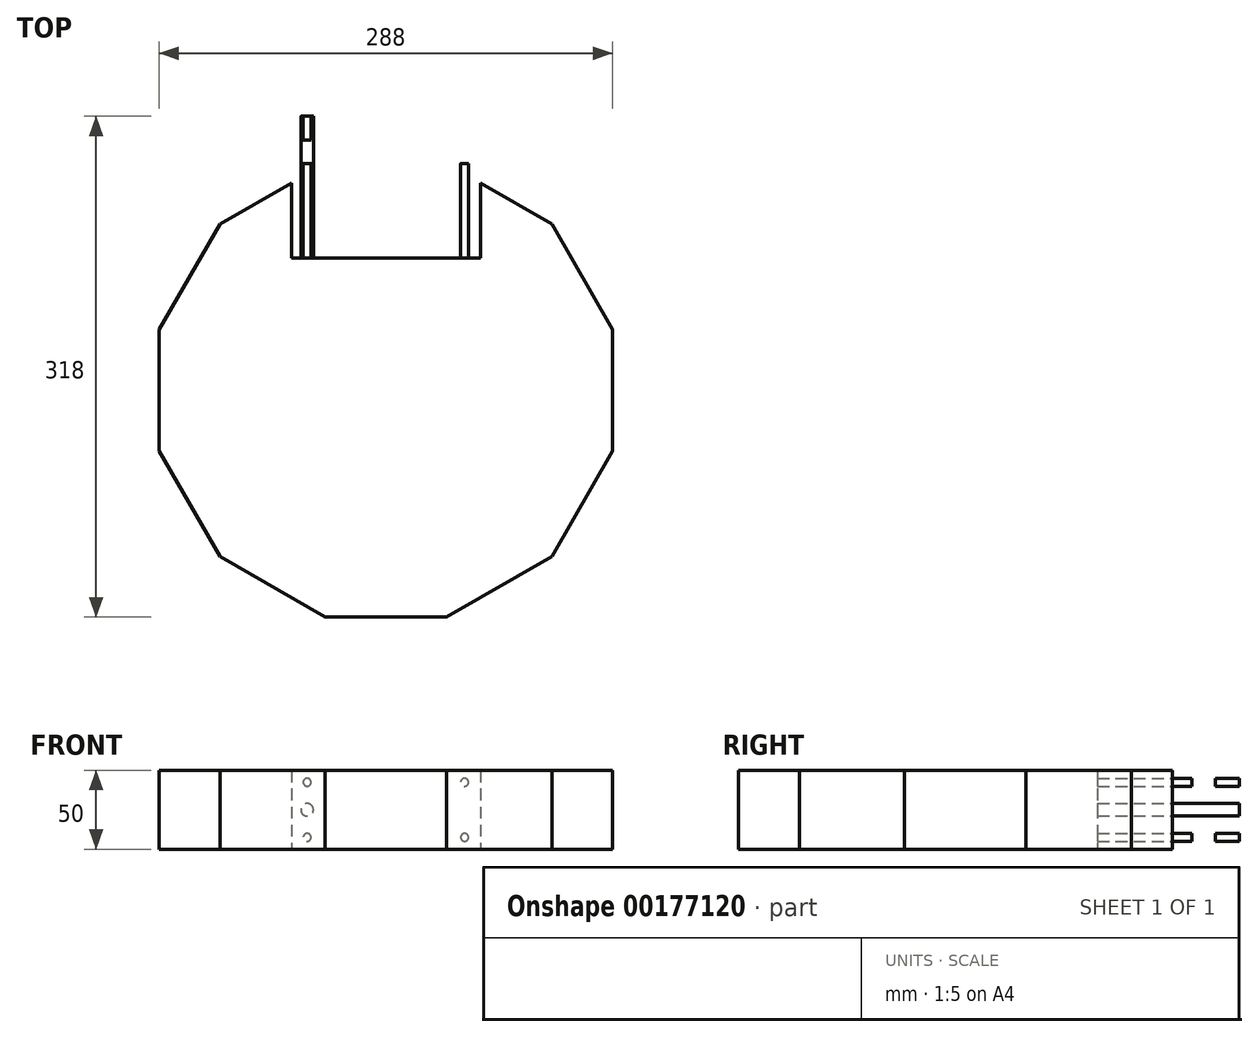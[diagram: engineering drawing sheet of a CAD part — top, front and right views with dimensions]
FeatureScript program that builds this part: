
annotation { "Feature Type Name" : "Feature", "Feature Type Description" : "" }
export const myFeature = defineFeature(function(context is Context, id is Id, definition is map)
    precondition{}
    {
        {
            var Q0;
            Q0=qCreatedBy(makeId("Top.planeOp"),FACE);
            var sketch = newSketch(context, id + "F0", { "sketchPlane" : qUnion([Q0])});
            skCircle(sketch, "E0.cCircle", {"center": v(0, 0) * mm, "radius": 144 * mm, "construction": true});
            skLineSegment(sketch, "E0.0", {"start": v(-38.58, 144) * mm, "end": v(38.58, 144) * mm, "construction": true});
            skLineSegment(sketch, "E0.1", {"start": v(38.58, 144) * mm, "end": v(105.42, 105.42) * mm, "construction": true});
            skLineSegment(sketch, "E0.2", {"start": v(105.42, 105.42) * mm, "end": v(144, 38.58) * mm});
            skLineSegment(sketch, "E0.3", {"start": v(144, 38.58) * mm, "end": v(144, -38.58) * mm});
            skLineSegment(sketch, "E0.4", {"start": v(144, -38.58) * mm, "end": v(105.42, -105.42) * mm});
            skLineSegment(sketch, "E0.5", {"start": v(105.42, -105.42) * mm, "end": v(38.58, -144) * mm});
            skLineSegment(sketch, "E0.6", {"start": v(38.58, -144) * mm, "end": v(-38.58, -144) * mm});
            skLineSegment(sketch, "E0.7", {"start": v(-38.58, -144) * mm, "end": v(-105.42, -105.42) * mm});
            skLineSegment(sketch, "E0.8", {"start": v(-105.42, -105.42) * mm, "end": v(-144, -38.58) * mm});
            skLineSegment(sketch, "E0.9", {"start": v(-144, -38.58) * mm, "end": v(-144, 38.58) * mm});
            skLineSegment(sketch, "E0.10", {"start": v(-144, 38.58) * mm, "end": v(-105.42, 105.42) * mm});
            skLineSegment(sketch, "E0.11", {"start": v(-105.42, 105.42) * mm, "end": v(-38.58, 144) * mm, "construction": true});
            skPoint(sketch, "E0.0.midPoint", {"position": v(0, 144) * mm});
            skLineSegment(sketch, "E1", {"start": v(-60, 174) * mm, "end": v(60, 174) * mm});
            skLineSegment(sketch, "E2", {"start": v(0, 0) * mm, "end": v(0, 217.16) * mm, "construction": true});
            skLineSegment(sketch, "E3", {"start": v(-60, 174) * mm, "end": v(-60, 131.64) * mm});
            skLineSegment(sketch, "E4", {"start": v(-60, 131.64) * mm, "end": v(-105.42, 105.42) * mm});
            skLineSegment(sketch, "E5", {"start": v(60, 174) * mm, "end": v(60, 131.64) * mm});
            skLineSegment(sketch, "E6", {"start": v(60, 131.64) * mm, "end": v(105.42, 105.42) * mm});
            skSolve(sketch);
        }
        {
            var Q0;
            Q0=makeQuery(id+"F0.imprint","IMPRINT",FACE,{"disambiguationData":[TD([[makeQuery(id+"F0.imprint","IMPRINT",EDGE,{"derivedFrom":sQuery(id+"F0.wireOp",EDGE,"E0.2")}),-1.0]])]});
            extrude(context, id + "F1", {"entities" : qUnion([Q0]), "depth" : 50 * mm});
        }
        {
            var Q0;
            Q0=makeQuery(id+"F1.opExtrude","CAP_FACE",FACE,{"disambiguationData":[OSD([sQuery(id+"F0.wireOp",EDGE,"E0.2"),sQuery(id+"F0.wireOp",EDGE,"E0.3"),sQuery(id+"F0.wireOp",EDGE,"E0.4"),sQuery(id+"F0.wireOp",EDGE,"E0.5"),sQuery(id+"F0.wireOp",EDGE,"E0.6"),sQuery(id+"F0.wireOp",EDGE,"E0.7"),sQuery(id+"F0.wireOp",EDGE,"E0.8"),sQuery(id+"F0.wireOp",EDGE,"E0.9"),sQuery(id+"F0.wireOp",EDGE,"E0.10"),sQuery(id+"F0.wireOp",EDGE,"E1"),sQuery(id+"F0.wireOp",EDGE,"E3"),sQuery(id+"F0.wireOp",EDGE,"E4"),sQuery(id+"F0.wireOp",EDGE,"E5"),sQuery(id+"F0.wireOp",EDGE,"E6")])],"isStart":false});
            var sketch = newSketch(context, id + "F2", { "sketchPlane" : qUnion([Q0])});
            skLineSegment(sketch, "E7", {"start": v(-60, 159) * mm, "end": v(-40, 159) * mm});
            skLineSegment(sketch, "E8", {"start": v(-60, 144) * mm, "end": v(-40, 144) * mm});
            skArc(sketch, "E9", {"start": v(-40, 144) * mm, "mid": v(-32.5, 151.5) * mm, "end": v(-40, 159) * mm});
            skLineSegment(sketch, "E10", {"start": v(-40, 159) * mm, "end": v(-40, 144) * mm, "construction": true});
            skLineSegment(sketch, "E11", {"start": v(-60, 151.5) * mm, "end": v(-40, 151.5) * mm, "construction": true});
            skLineSegment(sketch, "E12", {"start": v(-60, 159) * mm, "end": v(-60, 144) * mm});
            skLineSegment(sketch, "E13.MirrorCS", {"start": v(60, 159) * mm, "end": v(60, 144) * mm});
            skLineSegment(sketch, "E14.MirrorCS", {"start": v(60, 159) * mm, "end": v(40, 159) * mm});
            skArc(sketch, "E15.MirrorCS", {"start": v(40, 144) * mm, "mid": v(32.5, 151.5) * mm, "end": v(40, 159) * mm});
            skLineSegment(sketch, "E16.MirrorCS", {"start": v(60, 144) * mm, "end": v(40, 144) * mm});
            skCircle(sketch, "E17", {"center": v(0, 0) * mm, "radius": 87.5 * mm, "construction": true});
            skCircle(sketch, "E18", {"center": v(0, 87.5) * mm, "radius": 4 * mm});
            skCircle(sketch, "E19", {"center": v(50, 71.8) * mm, "radius": 4 * mm});
            skCircle(sketch, "E20", {"center": v(-50, 71.8) * mm, "radius": 4 * mm});
            skLineSegment(sketch, "E21", {"start": v(0, 87.5) * mm, "end": v(0, 0) * mm, "construction": true});
            skSolve(sketch);
        }
        {
            var Q0;
            Q0=makeQuery(id+"F2.imprint","IMPRINT",FACE,{"disambiguationData":[TD([[makeQuery(id+"F2.imprint","IMPRINT",EDGE,{"derivedFrom":sQuery(id+"F2.wireOp",EDGE,"E7")}),-1.0]])]});
            var Q1;
            Q1=makeQuery(id+"F2.imprint","IMPRINT",FACE,{"disambiguationData":[TD([[makeQuery(id+"F2.imprint","IMPRINT",EDGE,{"derivedFrom":sQuery(id+"F2.wireOp",EDGE,"E13.MirrorCS")}),-1.0]])]});
            extrude(context, id + "F3", {"entities" : qUnion([Q0, Q1]), "operationType" : NewBodyOperationType.REMOVE, "oppositeDirection" : true, "depth" : 15 * mm});
        }
        {
            var Q0;
            Q0=makeQuery(id+"F0.imprint","IMPRINT",FACE,{"disambiguationData":[TD([[makeQuery(id+"F0.imprint","IMPRINT",EDGE,{"derivedFrom":sQuery(id+"F0.wireOp",EDGE,"E0.2")}),-1.0]])]});
            var sketch = newSketch(context, id + "F4", { "sketchPlane" : qUnion([Q0])});
            skLineSegment(sketch, "E22.0", {"start": v(-60, 159) * mm, "end": v(-40, 159) * mm});
            skLineSegment(sketch, "E23.0", {"start": v(-60, 144) * mm, "end": v(-40, 144) * mm});
            skLineSegment(sketch, "E24.0", {"start": v(-60, 159) * mm, "end": v(-60, 144) * mm});
            skArc(sketch, "E25.0", {"start": v(-40, 144) * mm, "mid": v(-32.5, 151.5) * mm, "end": v(-40, 159) * mm});
            skLineSegment(sketch, "E26.0", {"start": v(60, 159) * mm, "end": v(40, 159) * mm});
            skArc(sketch, "E27.0", {"start": v(40, 144) * mm, "mid": v(32.5, 151.5) * mm, "end": v(40, 159) * mm});
            skLineSegment(sketch, "E28.0", {"start": v(60, 144) * mm, "end": v(40, 144) * mm});
            skLineSegment(sketch, "E29.0", {"start": v(60, 159) * mm, "end": v(60, 144) * mm});
            skSolve(sketch);
        }
        {
            var Q0;
            Q0=makeQuery(id+"F4.imprint","IMPRINT",FACE,{"disambiguationData":[TD([[makeQuery(id+"F4.imprint","IMPRINT",EDGE,{"derivedFrom":sQuery(id+"F4.wireOp",EDGE,"E26.0")}),1.0]])]});
            var Q1;
            Q1=makeQuery(id+"F4.imprint","IMPRINT",FACE,{"disambiguationData":[TD([[makeQuery(id+"F4.imprint","IMPRINT",EDGE,{"derivedFrom":sQuery(id+"F4.wireOp",EDGE,"E22.0")}),-1.0]])]});
            extrude(context, id + "F5", {"entities" : qUnion([Q0, Q1]), "operationType" : NewBodyOperationType.REMOVE, "depth" : 15 * mm});
        }
        {
            var Q0;
            Q0=makeQuery(id+"F1.opExtrude","SWEPT_FACE",FACE,{"disambiguationData":[OSD([sQuery(id+"F0.wireOp",EDGE,"E1")])]});
            var sketch = newSketch(context, id + "F6", { "sketchPlane" : qUnion([Q0])});
            skLineSegment(sketch, "E30", {"start": v(-60, 25) * mm, "end": v(60, 25) * mm, "construction": true});
            skLineSegment(sketch, "E31", {"start": v(0, 0) * mm, "end": v(0, 50) * mm, "construction": true});
            skCircle(sketch, "E32", {"center": v(-50, 25) * mm, "radius": 4 * mm});
            skCircle(sketch, "E33", {"center": v(-50, 42.5) * mm, "radius": 2.5 * mm});
            skCircle(sketch, "E34", {"center": v(-50, 7.5) * mm, "radius": 2.5 * mm});
            skLineSegment(sketch, "E35", {"start": v(-50, 50) * mm, "end": v(-50, 0) * mm, "construction": true});
            skCircle(sketch, "E36.MirrorC", {"center": v(50, 42.5) * mm, "radius": 2.5 * mm});
            skCircle(sketch, "E37.MirrorC", {"center": v(50, 25) * mm, "radius": 4 * mm});
            skCircle(sketch, "E38.MirrorC", {"center": v(50, 7.5) * mm, "radius": 2.5 * mm});
            skSolve(sketch);
        }
        {
            var Q0;
            Q0=makeQuery(id+"F6.imprint","IMPRINT",FACE,{"disambiguationData":[TD([[makeQuery(id+"F6.imprint","IMPRINT",EDGE,{"derivedFrom":sQuery(id+"F6.wireOp",EDGE,"E32")}),1.0]])]});
            var Q1;
            Q1=makeQuery(id+"F6.imprint","IMPRINT",FACE,{"disambiguationData":[TD([[makeQuery(id+"F6.imprint","IMPRINT",EDGE,{"derivedFrom":sQuery(id+"F6.wireOp",EDGE,"E37.MirrorC")}),-1.0]])]});
            extrude(context, id + "F7", {"entities" : qUnion([Q0, Q1]), "operationType" : NewBodyOperationType.REMOVE, "oppositeDirection" : true, "depth" : 90 * mm});
        }
        {
            var Q0;
            Q0=makeQuery(id+"F6.imprint","IMPRINT",FACE,{"disambiguationData":[TD([[makeQuery(id+"F6.imprint","IMPRINT",EDGE,{"derivedFrom":sQuery(id+"F6.wireOp",EDGE,"E33")}),1.0]])]});
            var Q1;
            Q1=makeQuery(id+"F6.imprint","IMPRINT",FACE,{"disambiguationData":[TD([[makeQuery(id+"F6.imprint","IMPRINT",EDGE,{"derivedFrom":sQuery(id+"F6.wireOp",EDGE,"E34")}),1.0]])]});
            var Q2;
            Q2=makeQuery(id+"F6.imprint","IMPRINT",FACE,{"disambiguationData":[TD([[makeQuery(id+"F6.imprint","IMPRINT",EDGE,{"derivedFrom":sQuery(id+"F6.wireOp",EDGE,"E38.MirrorC")}),-1.0]])]});
            var Q3;
            Q3=makeQuery(id+"F6.imprint","IMPRINT",FACE,{"disambiguationData":[TD([[makeQuery(id+"F6.imprint","IMPRINT",EDGE,{"derivedFrom":sQuery(id+"F6.wireOp",EDGE,"E36.MirrorC")}),-1.0]])]});
            extrude(context, id + "F8", {"entities" : qUnion([Q0, Q1, Q2, Q3]), "operationType" : NewBodyOperationType.REMOVE, "endBound" : BoundingType.UP_TO_NEXT, "oppositeDirection" : true, "depth" : 25 * mm});
        }
    });
